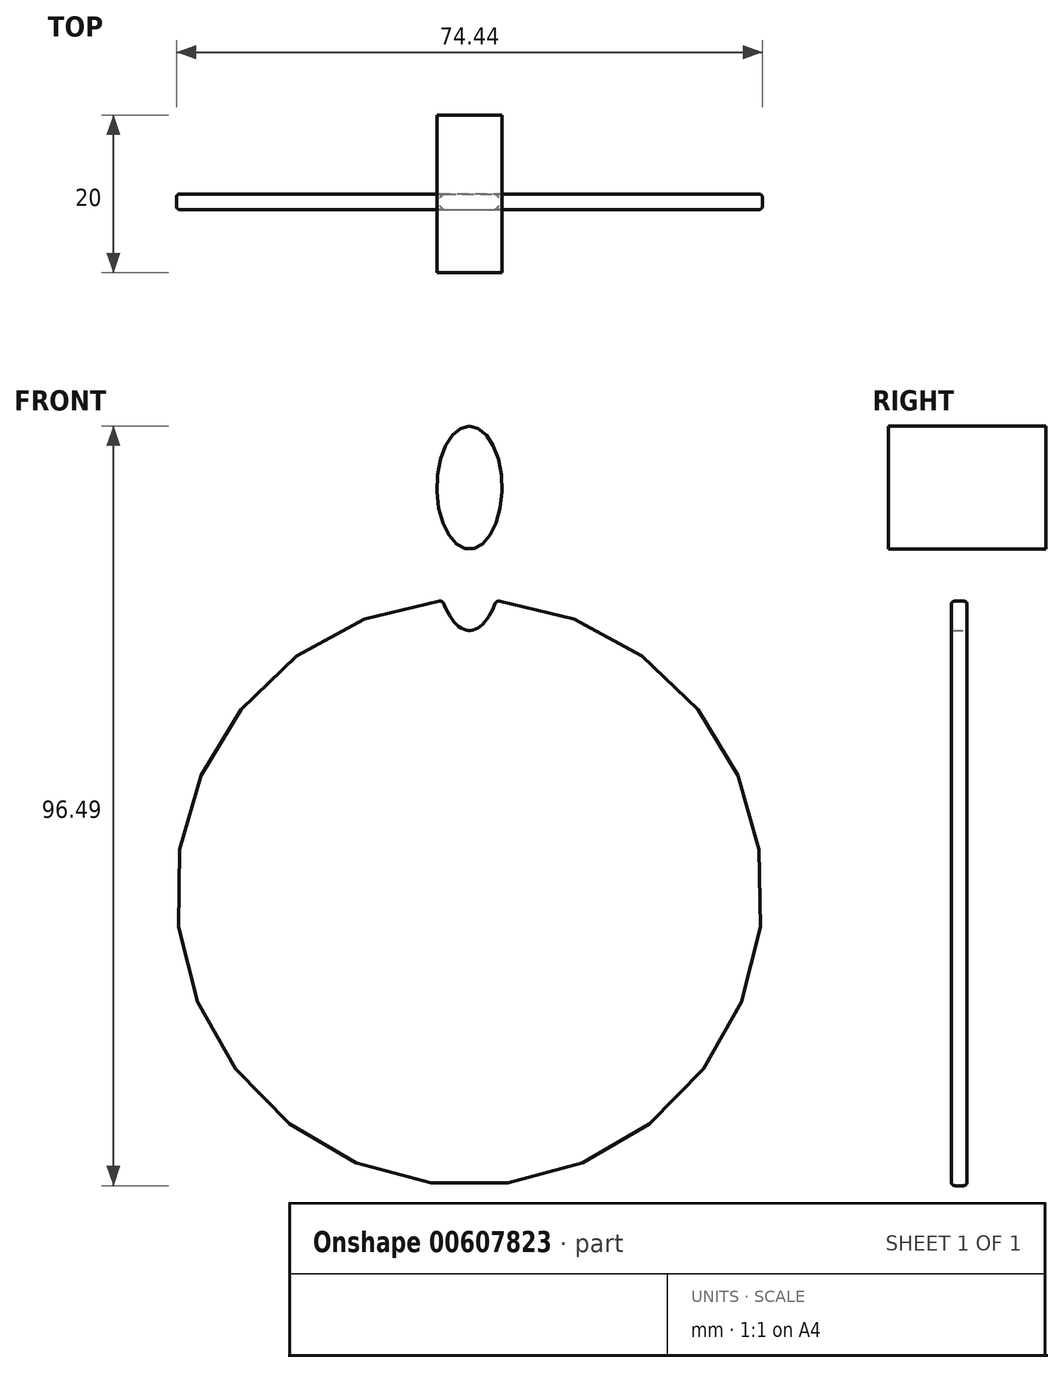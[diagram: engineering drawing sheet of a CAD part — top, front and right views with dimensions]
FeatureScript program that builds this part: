
annotation { "Feature Type Name" : "Feature", "Feature Type Description" : "" }
export const myFeature = defineFeature(function(context is Context, id is Id, definition is map)
    precondition{}
    {
        {
            var Q0;
            Q0=qCreatedBy(makeId("Front.planeOp"),FACE);
            var sketch = newSketch(context, id + "F0", { "sketchPlane" : qUnion([Q0])});
            skCircle(sketch, "E0", {"center": v(0, 0) * mm, "radius": 37.22 * mm});
            skSolve(sketch);
        }
        {
            var Q0;
            Q0 = qSketchRegion(id + "F0", true);
            extrude(context, id + "F1", {"entities" : qUnion([Q0]), "depth" : 2 * mm, "offsetDistance" : 25 * mm});
        }
        {
            var Q0;
            Q0=qCreatedBy(makeId("Front.planeOp"),FACE);
            var sketch = newSketch(context, id + "F2", { "sketchPlane" : qUnion([Q0])});
            skEllipse(sketch, "E1", {"center": v(0, 44.76) * mm, "majorRadius": 11.44 * mm, "minorRadius": 4.58 * mm, "majorAxis": v(0, -1)});
            skSolve(sketch);
        }
        {
            var Q0;
            Q0 = qSketchRegion(id + "F2", true);
            extrude(context, id + "F3", {"entities" : qUnion([Q0]), "operationType" : NewBodyOperationType.REMOVE, "endBound" : BoundingType.SYMMETRIC, "oppositeDirection" : true, "depth" : 25 * mm, "offsetDistance" : 25 * mm});
        }
        {
            var Q0;
            Q0=makeQuery(id+"F1.opExtrude","SWEPT_FACE",FACE,{"disambiguationData":[OSD([sQuery(id+"F0.wireOp",EDGE,"E0")])]});
            fillet(context, id + "F4", {"entities" : qUnion([Q0]), "radius" : 0.5 * mm, "tangentPropagation" : true, "rho" : 0.5, "crossSection" : FilletCrossSection.CONIC, "allowEdgeOverflow" : false});
        }
        {
            var Q0;
            Q0=qCreatedBy(makeId("Front.planeOp"),FACE);
            var sketch = newSketch(context, id + "F5", { "sketchPlane" : qUnion([Q0])});
            skArc(sketch, "E2", {"start": v(3.9, 54.05) * mm, "mid": v(9.95, 58.48) * mm, "end": v(2.5, 57.69) * mm});
            skLineSegment(sketch, "E3", {"start": v(-10.06, 60.96) * mm, "end": v(6.33, 60.96) * mm});
            skEllipse(sketch, "E4", {"center": v(0, 51.47) * mm, "majorRadius": 7.8 * mm, "minorRadius": 4.14 * mm, "majorAxis": v(0, 1)});
            skArc(sketch, "E5.MirrorCS", {"start": v(-3.9, 54.05) * mm, "mid": v(-9.95, 58.48) * mm, "end": v(-2.5, 57.69) * mm});
            skSolve(sketch);
        }
        {
            var Q0;
            {var subQ0=sQuery(id+"F5.wireOp",EDGE,"E5.MirrorCS");var subQ1=sQuery(id+"F5.wireOp",EDGE,"E4");var subQ2=makeQuery(id+"F5.imprint","INTERSECT",VERTEX,{"disambiguationData":[OD(0.0)],"derivedFrom":[subQ1,subQ0]});Q0=makeQuery(id+"F5.imprint","IMPRINT",FACE,{"disambiguationData":[TD([[makeQuery(id+"F5.imprint","IMPRINT",EDGE,{"disambiguationData":[TD([[subQ2,1.0]])],"derivedFrom":subQ1}),1.0]])]});}
            extrude(context, id + "F6", {"entities" : qUnion([Q0]), "endBound" : BoundingType.SYMMETRIC, "depth" : 20 * mm, "offsetDistance" : 25 * mm});
        }
    });
